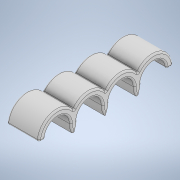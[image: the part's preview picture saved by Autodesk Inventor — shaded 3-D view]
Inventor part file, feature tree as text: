
AUTODESK INVENTOR PART (.ipt)
format: ipt  version: 2020 (Build 240168000, 168)  size: 279,040 bytes
history: native  units: in
note: dims shown in document units (in); Inventor stores cm internally (conversion verified against a paired STEP export)
features: fillet x3, extrude x1, sketch x1
ambient origin geometry x8: Origin, YZ Plane, XZ Plane, XY Plane, X Axis, Y Axis, Z Axis, Center Point
bodies: Solid1 (feature_tree)
feature tree (5):
  extrude  "Extrusion1"  Depth=0.315in
  fillet  "Fillet1"  Radius=1.5748in
  fillet  "Fillet2"  Radius=0.3937in
  fillet  "Fillet3"  Radius=0.0118in
  sketch  "Sketch1"  dims[d0=0.4724in d1=0.315in d2=1.5748in d4=0.3937in d5=0.3937in d7=1.0in d9=0.3937in d10=0.0in d11=0.0118in d12=0.0236in d13=0.0197in]
